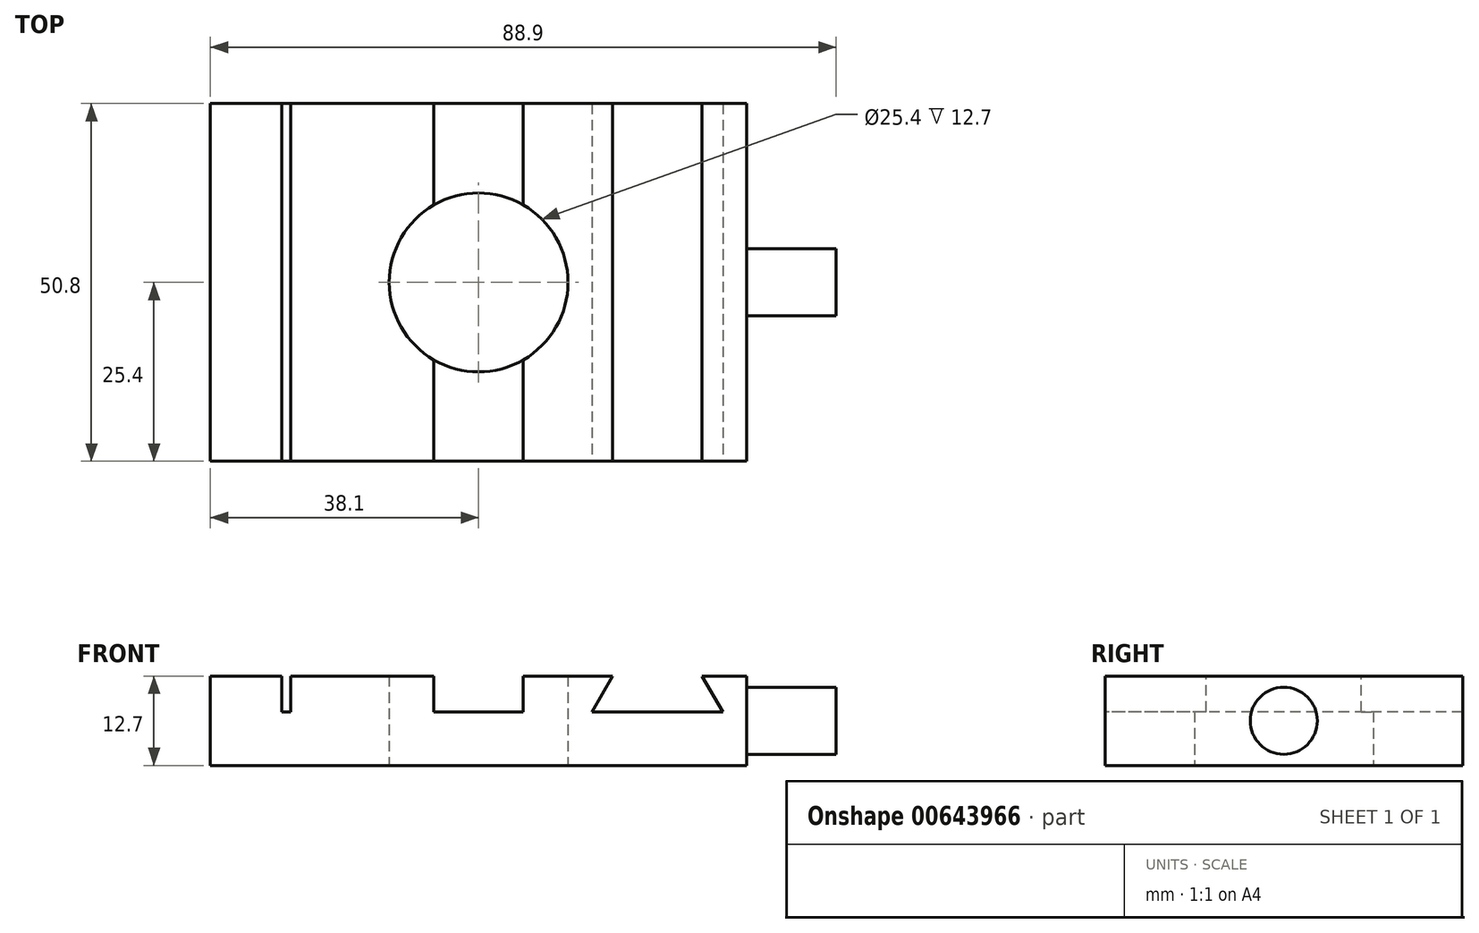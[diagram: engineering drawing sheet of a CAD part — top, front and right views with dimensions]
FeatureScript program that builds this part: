
annotation { "Feature Type Name" : "Feature", "Feature Type Description" : "" }
export const myFeature = defineFeature(function(context is Context, id is Id, definition is map)
    precondition{}
    {
        {
            var Q0;
            Q0=qCreatedBy(makeId("Top.planeOp"),FACE);
            var sketch = newSketch(context, id + "F0", { "sketchPlane" : qUnion([Q0])});
            skLineSegment(sketch, "E0.bottom", {"start": v(38.1, 25.4) * mm, "end": v(-38.1, 25.4) * mm});
            skLineSegment(sketch, "E0.top", {"start": v(38.1, -25.4) * mm, "end": v(-38.1, -25.4) * mm});
            skLineSegment(sketch, "E0.left", {"start": v(38.1, 25.4) * mm, "end": v(38.1, -25.4) * mm});
            skLineSegment(sketch, "E0.right", {"start": v(-38.1, 25.4) * mm, "end": v(-38.1, -25.4) * mm});
            skPoint(sketch, "E0.middle", {"position": v(0, 0) * mm});
            skCircle(sketch, "E1", {"center": v(0, 0) * mm, "radius": 12.7 * mm});
            skSolve(sketch);
        }
        {
            var Q0;
            Q0=makeQuery(id+"F0.imprint","IMPRINT",FACE,{"disambiguationData":[TD([[makeQuery(id+"F0.imprint","IMPRINT",EDGE,{"derivedFrom":sQuery(id+"F0.wireOp",EDGE,"E0.bottom")}),1.0]])]});
            extrude(context, id + "F1", {"entities" : qUnion([Q0]), "depth" : 12.7 * mm, "offsetDistance" : 25.4 * mm});
        }
        {
            var Q0;
            Q0=makeQuery(id+"F1.opExtrude","CAP_FACE",FACE,{"disambiguationData":[OSD([sQuery(id+"F0.wireOp",EDGE,"E0.bottom"),sQuery(id+"F0.wireOp",EDGE,"E0.top"),sQuery(id+"F0.wireOp",EDGE,"E0.left"),sQuery(id+"F0.wireOp",EDGE,"E0.right"),sQuery(id+"F0.wireOp",EDGE,"E1")])],"isStart":false});
            var sketch = newSketch(context, id + "F2", { "sketchPlane" : qUnion([Q0])});
            skLineSegment(sketch, "E2.bottom", {"start": v(-27.94, 25.4) * mm, "end": v(-26.67, 25.4) * mm});
            skLineSegment(sketch, "E2.top", {"start": v(-27.94, -25.4) * mm, "end": v(-26.67, -25.4) * mm});
            skLineSegment(sketch, "E2.left", {"start": v(-27.94, 25.4) * mm, "end": v(-27.94, -25.4) * mm});
            skLineSegment(sketch, "E2.right", {"start": v(-26.67, 25.4) * mm, "end": v(-26.67, -25.4) * mm});
            skLineSegment(sketch, "E3", {"start": v(-6.35, 25.4) * mm, "end": v(-6.35, -25.4) * mm});
            skLineSegment(sketch, "E4", {"start": v(6.35, 25.4) * mm, "end": v(6.35, -25.4) * mm});
            skPoint(sketch, "E5", {"position": v(0, 0) * mm});
            skLineSegment(sketch, "E6", {"start": v(-6.35, -25.4) * mm, "end": v(6.35, -25.4) * mm});
            skLineSegment(sketch, "E7", {"start": v(-6.35, 25.4) * mm, "end": v(6.35, 25.4) * mm});
            skLineSegment(sketch, "E8", {"start": v(0, 25.4) * mm, "end": v(0, -25.4) * mm, "construction": true});
            skSolve(sketch);
        }
        {
            var Q0;
            Q0=makeQuery(id+"F2.imprint","IMPRINT",FACE,{"disambiguationData":[TD([[makeQuery(id+"F2.imprint","IMPRINT",EDGE,{"derivedFrom":sQuery(id+"F2.wireOp",EDGE,"E2.bottom")}),1.0]])]});
            var Q1;
            {var subQ0=sQuery(id+"F2.wireOp",EDGE,"E7");Q1=makeQuery(id+"F2.imprint","IMPRINT",FACE,{"disambiguationData":[TD([[makeQuery(id+"F2.imprint","IMPRINT",EDGE,{"derivedFrom":subQ0}),1.0]])]});}
            var Q2;
            {var subQ0=sQuery(id+"F2.wireOp",EDGE,"E6");Q2=makeQuery(id+"F2.imprint","IMPRINT",FACE,{"disambiguationData":[TD([[makeQuery(id+"F2.imprint","IMPRINT",EDGE,{"derivedFrom":subQ0}),-1.0]])]});}
            extrude(context, id + "F3", {"entities" : qUnion([Q0, Q1, Q2]), "operationType" : NewBodyOperationType.REMOVE, "oppositeDirection" : true, "depth" : 5.08 * mm, "offsetDistance" : 25 * mm});
        }
        {
            var Q0;
            Q0=makeQuery(id+"F1.opExtrude","SWEPT_FACE",FACE,{"disambiguationData":[OSD([sQuery(id+"F0.wireOp",EDGE,"E0.top")])]});
            var sketch = newSketch(context, id + "F4", { "sketchPlane" : qUnion([Q0])});
            skLineSegment(sketch, "E9", {"start": v(19.05, 12.7) * mm, "end": v(16.12, 7.62) * mm});
            skLineSegment(sketch, "E10", {"start": v(16.12, 7.62) * mm, "end": v(34.68, 7.62) * mm});
            skLineSegment(sketch, "E11", {"start": v(34.68, 7.62) * mm, "end": v(31.75, 12.7) * mm});
            skLineSegment(sketch, "E12", {"start": v(31.75, 12.7) * mm, "end": v(19.05, 12.7) * mm});
            skLineSegment(sketch, "E13", {"start": v(19.05, 12.7) * mm, "end": v(31.75, 12.7) * mm});
            skLineSegment(sketch, "E14", {"start": v(34.68, 7.62) * mm, "end": v(16.12, 7.62) * mm});
            skLineSegment(sketch, "E15", {"start": v(25.4, 7.62) * mm, "end": v(25.4, 12.7) * mm, "construction": true});
            skSolve(sketch);
        }
        {
            var Q0;
            Q0=makeQuery(id+"F4.imprint","IMPRINT",FACE,{"disambiguationData":[TD([[makeQuery(id+"F4.imprint","IMPRINT",EDGE,{"derivedFrom":sQuery(id+"F4.wireOp",EDGE,"E9")}),1.0]])]});
            extrude(context, id + "F5", {"entities" : qUnion([Q0]), "operationType" : NewBodyOperationType.REMOVE, "endBound" : BoundingType.THROUGH_ALL, "oppositeDirection" : true, "depth" : 25 * mm, "offsetDistance" : 25 * mm});
        }
        {
            var Q0;
            Q0=makeQuery(id+"F1.opExtrude","SWEPT_FACE",FACE,{"disambiguationData":[OSD([sQuery(id+"F0.wireOp",EDGE,"E0.left")])]});
            var sketch = newSketch(context, id + "F6", { "sketchPlane" : qUnion([Q0])});
            skCircle(sketch, "E16", {"center": v(0, 6.35) * mm, "radius": 4.76 * mm});
            skPoint(sketch, "E17", {"position": v(-25.4, 6.35) * mm});
            skSolve(sketch);
        }
        {
            var Q0;
            Q0=makeQuery(id+"F6.imprint","IMPRINT",FACE,{"disambiguationData":[TD([[makeQuery(id+"F6.imprint","IMPRINT",EDGE,{"derivedFrom":sQuery(id+"F6.wireOp",EDGE,"E16")}),1.0]])]});
            extrude(context, id + "F7", {"entities" : qUnion([Q0]), "operationType" : NewBodyOperationType.ADD, "depth" : 12.7 * mm, "offsetDistance" : 25 * mm});
        }
    });
